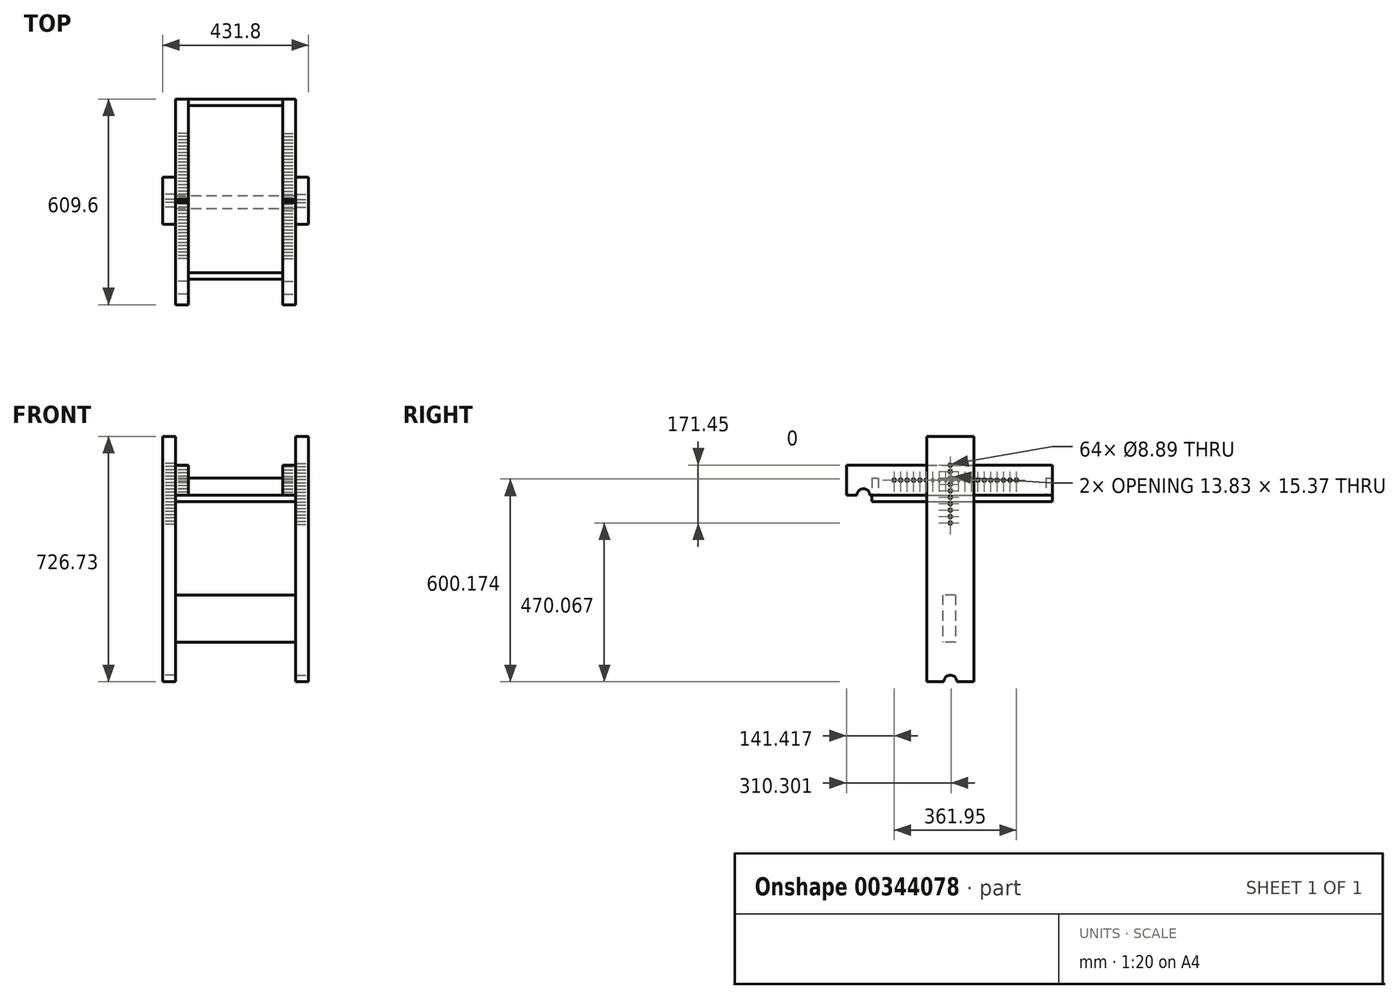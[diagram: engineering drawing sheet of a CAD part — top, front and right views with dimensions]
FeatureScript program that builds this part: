
annotation { "Feature Type Name" : "Feature", "Feature Type Description" : "" }
export const myFeature = defineFeature(function(context is Context, id is Id, definition is map)
    precondition{}
    {
        {
            var Q0;
            Q0=qCreatedBy(makeId("Right.planeOp"),FACE);
            var sketch = newSketch(context, id + "F0", { "sketchPlane" : qUnion([Q0])});
            skLineSegment(sketch, "E0", {"start": v(-273.03, 718.1) * mm, "end": v(285.89, -480.5) * mm, "construction": true});
            skLineSegment(sketch, "E1", {"start": v(-191.78, 754.22) * mm, "end": v(359.92, -428.91) * mm, "construction": true});
            skLineSegment(sketch, "E2", {"start": v(285.89, -480.5) * mm, "end": v(-310.41, -480.5) * mm, "construction": true});
            skLineSegment(sketch, "E3", {"start": v(-170.79, 498.85) * mm, "end": v(-90.22, 536.42) * mm, "construction": true});
            skCircle(sketch, "E4", {"center": v(-130.5, 517.63) * mm, "radius": 19.05 * mm, "construction": true});
            skLineSegment(sketch, "E5", {"start": v(86.84, -53.64) * mm, "end": v(167.41, -16.07) * mm, "construction": true});
            skCircle(sketch, "E6", {"center": v(127.13, -34.85) * mm, "radius": 19.05 * mm, "construction": true});
            skSolve(sketch);
        }
        {
            var Q0;
            Q0=qCreatedBy(makeId("Right.planeOp"),FACE);
            var sketch = newSketch(context, id + "F1", { "sketchPlane" : qUnion([Q0])});
            skLineSegment(sketch, "E7.bottom", {"start": v(-180.61, 606.53) * mm, "end": v(428.99, 606.53) * mm});
            skLineSegment(sketch, "E7.top", {"start": v(-180.61, 517.63) * mm, "end": v(428.99, 517.63) * mm});
            skLineSegment(sketch, "E7.left", {"start": v(-180.61, 606.53) * mm, "end": v(-180.61, 517.63) * mm});
            skLineSegment(sketch, "E7.right", {"start": v(428.99, 606.53) * mm, "end": v(428.99, 517.63) * mm});
            skSolve(sketch);
        }
        {
            var Q0;
            Q0=qSketchRegion(id+"F1",true);
            extrude(context, id + "F2", {"entities" : qUnion([Q0]), "oppositeDirection" : true, "depth" : 38.1 * mm});
        }
        {
            var Q0;
            Q0=makeQuery(id+"F2.opExtrude","CAP_FACE",FACE,{"disambiguationData":[OSD([sQuery(id+"F1.wireOp",EDGE,"E7.bottom"),sQuery(id+"F1.wireOp",EDGE,"E7.top"),sQuery(id+"F1.wireOp",EDGE,"E7.left"),sQuery(id+"F1.wireOp",EDGE,"E7.right")])],"isStart":true});
            var sketch = newSketch(context, id + "F3", { "sketchPlane" : qUnion([Q0])});
            skLineSegment(sketch, "E8", {"start": v(-180.61, 562.08) * mm, "end": v(428.99, 562.08) * mm, "construction": true});
            skCircle(sketch, "E9", {"center": v(-39.2, 562.08) * mm, "radius": 4.45 * mm});
            skCircle(sketch, "E10.1.0.0", {"center": v(-20.14, 562.08) * mm, "radius": 4.45 * mm});
            skCircle(sketch, "E10.2.0.0", {"center": v(-1.1, 562.08) * mm, "radius": 4.45 * mm});
            skCircle(sketch, "E10.3.0.0", {"center": v(17.96, 562.08) * mm, "radius": 4.45 * mm});
            skCircle(sketch, "E10.4.0.0", {"center": v(37, 562.08) * mm, "radius": 4.45 * mm});
            skCircle(sketch, "E10.5.0.0", {"center": v(56.06, 562.08) * mm, "radius": 4.45 * mm});
            skCircle(sketch, "E10.6.0.0", {"center": v(75.1, 562.08) * mm, "radius": 4.45 * mm});
            skCircle(sketch, "E10.7.0.0", {"center": v(94.16, 562.08) * mm, "radius": 4.45 * mm});
            skCircle(sketch, "E10.8.0.0", {"center": v(113.2, 562.08) * mm, "radius": 4.45 * mm});
            skCircle(sketch, "E10.9.0.0", {"center": v(132.26, 562.08) * mm, "radius": 4.45 * mm});
            skCircle(sketch, "E10.10.0.0", {"center": v(151.3, 562.08) * mm, "radius": 4.45 * mm});
            skCircle(sketch, "E10.11.0.0", {"center": v(170.36, 562.08) * mm, "radius": 4.45 * mm});
            skCircle(sketch, "E10.12.0.0", {"center": v(189.4, 562.08) * mm, "radius": 4.45 * mm});
            skCircle(sketch, "E10.13.0.0", {"center": v(208.46, 562.08) * mm, "radius": 4.45 * mm});
            skCircle(sketch, "E10.14.0.0", {"center": v(227.5, 562.08) * mm, "radius": 4.45 * mm});
            skCircle(sketch, "E10.15.0.0", {"center": v(246.56, 562.08) * mm, "radius": 4.45 * mm});
            skCircle(sketch, "E10.16.0.0", {"center": v(265.6, 562.08) * mm, "radius": 4.45 * mm});
            skCircle(sketch, "E10.17.0.0", {"center": v(284.66, 562.08) * mm, "radius": 4.45 * mm});
            skCircle(sketch, "E10.18.0.0", {"center": v(303.7, 562.08) * mm, "radius": 4.45 * mm});
            skCircle(sketch, "E10.19.0.0", {"center": v(322.76, 562.08) * mm, "radius": 4.45 * mm});
            skLineSegment(sketch, "E10.direction1", {"start": v(-39.2, 562.08) * mm, "end": v(-20.14, 562.08) * mm, "construction": true});
            skSolve(sketch);
        }
        {
            var Q0;
            Q0=qSketchRegion(id+"F3",true);
            extrude(context, id + "F4", {"entities" : qUnion([Q0]), "operationType" : NewBodyOperationType.REMOVE, "endBound" : BoundingType.THROUGH_ALL, "oppositeDirection" : true, "depth" : 25.4 * mm});
        }
        {
            var Q0;
            Q0=qCreatedBy(makeId("Right.planeOp"),FACE);
            var sketch = newSketch(context, id + "F5", { "sketchPlane" : qUnion([Q0])});
            skLineSegment(sketch, "E11.bottom", {"start": v(57.28, 691.88) * mm, "end": v(196.98, 691.88) * mm});
            skLineSegment(sketch, "E11.top", {"start": v(57.28, -34.85) * mm, "end": v(196.98, -34.85) * mm});
            skLineSegment(sketch, "E11.left", {"start": v(57.28, 691.88) * mm, "end": v(57.28, -34.85) * mm});
            skLineSegment(sketch, "E11.right", {"start": v(196.98, 691.88) * mm, "end": v(196.98, -34.85) * mm});
            skSolve(sketch);
        }
        {
            var Q0;
            Q0=qSketchRegion(id+"F5",true);
            extrude(context, id + "F6", {"entities" : qUnion([Q0]), "depth" : 38.1 * mm});
        }
        {
            var Q0;
            Q0=makeQuery(id+"F6.opExtrude","CAP_FACE",FACE,{"disambiguationData":[OSD([sQuery(id+"F5.wireOp",EDGE,"E11.bottom"),sQuery(id+"F5.wireOp",EDGE,"E11.top"),sQuery(id+"F5.wireOp",EDGE,"E11.left"),sQuery(id+"F5.wireOp",EDGE,"E11.right")])],"isStart":false});
            var sketch = newSketch(context, id + "F7", { "sketchPlane" : qUnion([Q0])});
            skLineSegment(sketch, "E12", {"start": v(127.13, 691.88) * mm, "end": v(127.13, 283.48) * mm, "construction": true});
            skCircle(sketch, "E13", {"center": v(127.13, 606.67) * mm, "radius": 4.45 * mm});
            skCircle(sketch, "E14.0.1.0", {"center": v(127.13, 587.62) * mm, "radius": 4.45 * mm});
            skCircle(sketch, "E14.0.2.0", {"center": v(127.13, 568.57) * mm, "radius": 4.45 * mm});
            skCircle(sketch, "E14.0.3.0", {"center": v(127.13, 549.52) * mm, "radius": 4.45 * mm});
            skCircle(sketch, "E14.0.4.0", {"center": v(127.13, 530.47) * mm, "radius": 4.45 * mm});
            skCircle(sketch, "E14.0.5.0", {"center": v(127.13, 511.42) * mm, "radius": 4.45 * mm});
            skCircle(sketch, "E14.0.6.0", {"center": v(127.13, 492.37) * mm, "radius": 4.45 * mm});
            skCircle(sketch, "E14.0.7.0", {"center": v(127.13, 473.32) * mm, "radius": 4.45 * mm});
            skCircle(sketch, "E14.0.8.0", {"center": v(127.13, 454.27) * mm, "radius": 4.45 * mm});
            skCircle(sketch, "E14.0.9.0", {"center": v(127.13, 435.22) * mm, "radius": 4.45 * mm});
            skLineSegment(sketch, "E14.direction1", {"start": v(127.13, 606.67) * mm, "end": v(149.47, 606.1) * mm, "construction": true});
            skLineSegment(sketch, "E14.direction2", {"start": v(127.13, 606.67) * mm, "end": v(127.13, 587.62) * mm, "construction": true});
            skSolve(sketch);
        }
        {
            var Q0;
            Q0=qSketchRegion(id+"F7",true);
            extrude(context, id + "F8", {"entities" : qUnion([Q0]), "operationType" : NewBodyOperationType.REMOVE, "endBound" : BoundingType.THROUGH_ALL, "oppositeDirection" : true, "depth" : 25.4 * mm});
        }
        {
            var Q0;
            {var subQ0=sQuery(id+"F1.wireOp",EDGE,"E7.left");var subQ1=sQuery(id+"F1.wireOp",EDGE,"E7.top");var subQ3=sQuery(id+"F1.wireOp",EDGE,"E7.bottom");Q0=makeQuery(id+"F6.boolean.opBoolean","SPLIT",FACE,{"disambiguationData":[TD([makeQuery(id+"F2.opExtrude","SWEPT_FACE",FACE,{"disambiguationData":[OSD([subQ0])]})])],"derivedFrom":makeQuery(id+"F2.opExtrude","CAP_FACE",FACE,{"disambiguationData":[OSD([subQ3,subQ1,subQ0,sQuery(id+"F1.wireOp",EDGE,"E7.right")])],"isStart":true})});}
            var sketch = newSketch(context, id + "F9", { "sketchPlane" : qUnion([Q0])});
            skCircle(sketch, "E15.0", {"center": v(-130.5, 517.63) * mm, "radius": 19.05 * mm});
            skSolve(sketch);
        }
        {
            var Q0;
            Q0=qSketchRegion(id+"F9",true);
            extrude(context, id + "F10", {"entities" : qUnion([Q0]), "operationType" : NewBodyOperationType.REMOVE, "endBound" : BoundingType.THROUGH_ALL, "oppositeDirection" : true, "depth" : 25.4 * mm});
        }
        {
            var Q0;
            Q0=makeQuery(id+"F6.opExtrude","CAP_FACE",FACE,{"disambiguationData":[OSD([sQuery(id+"F5.wireOp",EDGE,"E11.bottom"),sQuery(id+"F5.wireOp",EDGE,"E11.top"),sQuery(id+"F5.wireOp",EDGE,"E11.left"),sQuery(id+"F5.wireOp",EDGE,"E11.right")])],"isStart":false});
            var sketch = newSketch(context, id + "F11", { "sketchPlane" : qUnion([Q0])});
            skCircle(sketch, "E16.0", {"center": v(127.13, -34.85) * mm, "radius": 19.05 * mm});
            skSolve(sketch);
        }
        {
            var Q0;
            Q0=qSketchRegion(id+"F11",true);
            extrude(context, id + "F12", {"entities" : qUnion([Q0]), "operationType" : NewBodyOperationType.REMOVE, "endBound" : BoundingType.THROUGH_ALL, "oppositeDirection" : true, "depth" : 25.4 * mm});
        }
        {
            var Q0;
            Q0=makeQuery(id+"F2.opExtrude","CAP_FACE",FACE,{"disambiguationData":[OSD([sQuery(id+"F1.wireOp",EDGE,"E7.bottom"),sQuery(id+"F1.wireOp",EDGE,"E7.top"),sQuery(id+"F1.wireOp",EDGE,"E7.left"),sQuery(id+"F1.wireOp",EDGE,"E7.right")])],"isStart":true});
            var sketch = newSketch(context, id + "F13", { "sketchPlane" : qUnion([Q0])});
            skLineSegment(sketch, "E17.bottom", {"start": v(-105.1, 517.63) * mm, "end": v(428.99, 517.63) * mm});
            skLineSegment(sketch, "E17.top", {"start": v(-105.1, 498.58) * mm, "end": v(428.99, 498.58) * mm});
            skLineSegment(sketch, "E17.left", {"start": v(-105.1, 517.63) * mm, "end": v(-105.1, 498.58) * mm});
            skLineSegment(sketch, "E17.right", {"start": v(428.99, 517.63) * mm, "end": v(428.99, 498.58) * mm});
            skSolve(sketch);
        }
        {
            var Q0;
            Q0=qSketchRegion(id+"F13",true);
            extrude(context, id + "F14", {"entities" : qUnion([Q0]), "oppositeDirection" : true, "depth" : 355.6 * mm});
        }
        {
            var Q0;
            Q0=makeQuery(id+"F14.opExtrude","CAP_FACE",FACE,{"disambiguationData":[OSD([sQuery(id+"F13.wireOp",EDGE,"E17.bottom"),sQuery(id+"F13.wireOp",EDGE,"E17.top"),sQuery(id+"F13.wireOp",EDGE,"E17.left"),sQuery(id+"F13.wireOp",EDGE,"E17.right")])],"isStart":true});
            var Q1;
            Q1=makeQuery(id+"F14.opExtrude","CAP_FACE",FACE,{"disambiguationData":[OSD([sQuery(id+"F13.wireOp",EDGE,"E17.bottom"),sQuery(id+"F13.wireOp",EDGE,"E17.top"),sQuery(id+"F13.wireOp",EDGE,"E17.left"),sQuery(id+"F13.wireOp",EDGE,"E17.right")])],"isStart":false});
            cPlane(context, id + "F15", {"entities" : qUnion([Q0, Q1]), "cplaneType" : CPlaneType.MID_PLANE, "offset" : 25.4 * mm, "width" : 152.4 * mm, "height" : 152.4 * mm});
        }
        {
            var Q0;
            Q0=makeQuery(id+"F2.opExtrude","SWEPT_BODY",BODY,{"disambiguationData":[OSD([sQuery(id+"F1.wireOp",EDGE,"E7.bottom"),sQuery(id+"F1.wireOp",EDGE,"E7.top"),sQuery(id+"F1.wireOp",EDGE,"E7.left"),sQuery(id+"F1.wireOp",EDGE,"E7.right")])]});
            var Q1;
            Q1=makeQuery(id+"F6.opExtrude","SWEPT_BODY",BODY,{"disambiguationData":[OSD([sQuery(id+"F5.wireOp",EDGE,"E11.bottom"),sQuery(id+"F5.wireOp",EDGE,"E11.top"),sQuery(id+"F5.wireOp",EDGE,"E11.left"),sQuery(id+"F5.wireOp",EDGE,"E11.right")])]});
            var Q2;
            Q2=qCreatedBy(id+"F15.planeOp",FACE);
            mirror(context, id + "F16", {"entities" : qUnion([Q0, Q1]), "mirrorPlane" : qUnion([Q2])});
        }
        {
            var Q0;
            Q0=makeQuery(id+"F6.opExtrude","CAP_FACE",FACE,{"disambiguationData":[OSD([sQuery(id+"F5.wireOp",EDGE,"E11.bottom"),sQuery(id+"F5.wireOp",EDGE,"E11.top"),sQuery(id+"F5.wireOp",EDGE,"E11.left"),sQuery(id+"F5.wireOp",EDGE,"E11.right")])],"isStart":true});
            var sketch = newSketch(context, id + "F17", { "sketchPlane" : qUnion([Q0])});
            skLineSegment(sketch, "E18.bottom", {"start": v(-142.4, 221.73) * mm, "end": v(-104.3, 221.73) * mm});
            skLineSegment(sketch, "E18.top", {"start": v(-142.4, 82.03) * mm, "end": v(-104.3, 82.03) * mm});
            skLineSegment(sketch, "E18.left", {"start": v(-142.4, 221.73) * mm, "end": v(-142.4, 82.03) * mm});
            skLineSegment(sketch, "E18.right", {"start": v(-104.3, 221.73) * mm, "end": v(-104.3, 82.03) * mm});
            skSolve(sketch);
        }
        {
            var Q0;
            Q0=qSketchRegion(id+"F17",true);
            var Q1;
            Q1=makeQuery(id+"F16.opPattern","COPY",FACE,{"derivedFrom":makeQuery(id+"F6.opExtrude","CAP_FACE",FACE,{"disambiguationData":[OSD([sQuery(id+"F5.wireOp",EDGE,"E11.bottom"),sQuery(id+"F5.wireOp",EDGE,"E11.top"),sQuery(id+"F5.wireOp",EDGE,"E11.left"),sQuery(id+"F5.wireOp",EDGE,"E11.right")])],"isStart":true}),"instanceName":"1"});
            extrude(context, id + "F18", {"entities" : qUnion([Q0]), "endBound" : BoundingType.UP_TO_SURFACE, "endBoundEntityFace" : qUnion([Q1]), "depth" : 25.4 * mm});
        }
        {
            var Q0;
            Q0=makeQuery(id+"F14.opExtrude","SWEPT_FACE",FACE,{"disambiguationData":[OSD([sQuery(id+"F13.wireOp",EDGE,"E17.bottom")])]});
            var sketch = newSketch(context, id + "F19", { "sketchPlane" : qUnion([Q0])});
            skLineSegment(sketch, "E19.bottom", {"start": v(-317.5, -105.1) * mm, "end": v(-38.1, -105.1) * mm});
            skLineSegment(sketch, "E19.top", {"start": v(-317.5, -86.05) * mm, "end": v(-38.1, -86.05) * mm});
            skLineSegment(sketch, "E19.left", {"start": v(-317.5, -105.1) * mm, "end": v(-317.5, -86.05) * mm});
            skLineSegment(sketch, "E19.right", {"start": v(-38.1, -105.1) * mm, "end": v(-38.1, -86.05) * mm});
            skLineSegment(sketch, "E20.bottom", {"start": v(-317.5, 409.94) * mm, "end": v(-38.1, 409.94) * mm});
            skLineSegment(sketch, "E20.top", {"start": v(-317.5, 428.99) * mm, "end": v(-38.1, 428.99) * mm});
            skLineSegment(sketch, "E20.left", {"start": v(-317.5, 409.94) * mm, "end": v(-317.5, 428.99) * mm});
            skLineSegment(sketch, "E20.right", {"start": v(-38.1, 409.94) * mm, "end": v(-38.1, 428.99) * mm});
            skSolve(sketch);
        }
        {
            var Q0;
            Q0=qSketchRegion(id+"F19",true);
            extrude(context, id + "F20", {"entities" : qUnion([Q0]), "depth" : 50.8 * mm});
        }
    });
